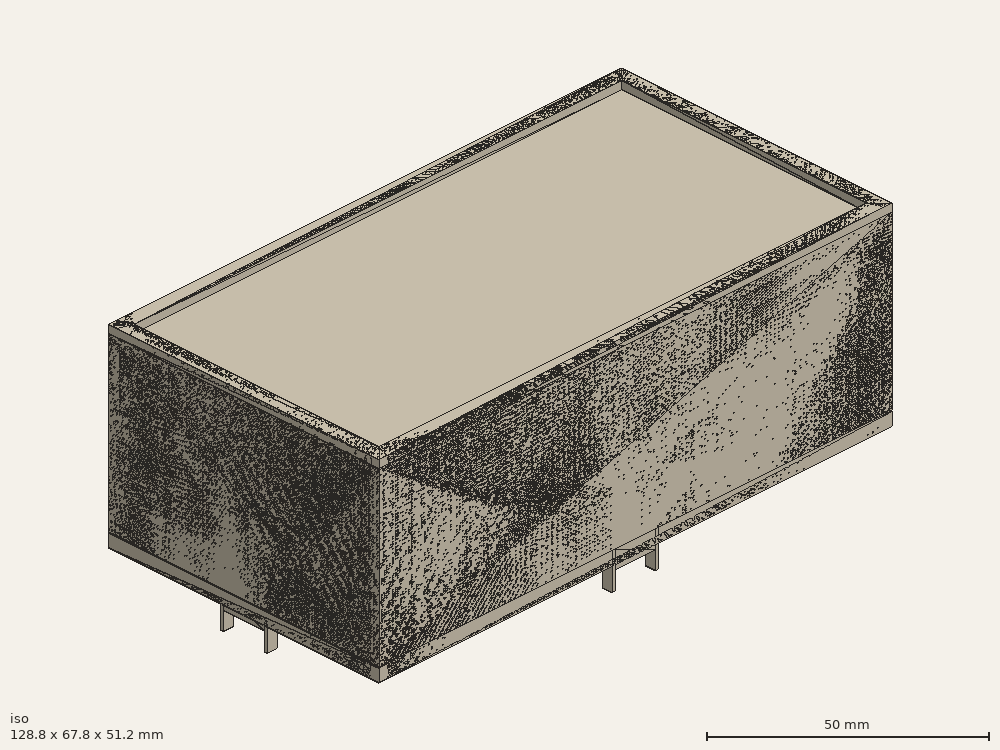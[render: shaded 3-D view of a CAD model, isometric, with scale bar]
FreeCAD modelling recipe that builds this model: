
FCSTD DOCUMENT  (FreeCAD 0.16R6712 (Git))
Label: DesKLOK_case_01
License: All rights reserved
LicenseURL: http://en.wikipedia.org/wiki/All_rights_reserved
objects: Part::Feature×98, Sketcher::SketchObject×19, PartDesign::Pad×15, App::DocumentObjectGroup×5, App::VRMLObject×3, PartDesign::Fillet×3, PartDesign::Pocket×3, Part::MultiFuse×2, PartDesign::LinearPattern×2, Mesh::Feature×1, PartDesign::MultiTransform×1
note: 161 computed .brp shape members not serialized (recipe doc carries the construction recipe); baked Part::Feature solids carry a one-line shape summary decoded from their .brp

FEATURE [App::VRMLObject] ultim8x8
  Placement = pos=(-30.48,0,0) rot=(0,0,1;0rad)
  Resources = ultim8x8/shapes3D/Cap_0805_2012.wrl | ultim8x8/shapes3D/cap_1210_3225M.wrl | ultim8x8/shapes3D/LED_SMD_APA102.wrl
FEATURE [App::VRMLObject] ultim8x8001  label="ultim8x009"
  Placement = pos=(30.48,0,0) rot=(0,0,1;0rad)
  Resources = ultim8x8001/shapes3D/Cap_0805_2012.wrl | ultim8x8001/shapes3D/cap_1210_3225M.wrl | ultim8x8001/shapes3D/LED_SMD_APA102.wrl
FEATURE [App::VRMLObject] ultim_bus_snapped
  Placement = pos=(0,0,-11.6002) rot=(0,1,0;3.14159rad)
  Resources = ultim_bus_snapped/shapes3D/r_0805.wrl
FEATURE [Part::Feature] Part__Feature  label="M0"
  Placement = pos=(-38.1,0,-17.8181) rot=(0.707107,-0.707107,0;3.14159rad)
  shape: bbox 22.93 x 51.59 x 14.94 mm, 1313 faces (baked)
FEATURE [Part::Feature] Part__Feature001  label="cap_elco_R100_D200_H460"
  Placement = pos=(-15.24,22.86,-10.668) rot=(1,0,0;3.14159rad)
  shape: bbox 6.114 x 6.114 x 15.1 mm, 124 faces (baked)
FEATURE [Part::Feature] Part__Feature002  label="User Library-PBS2-16_PBS2_1"
  shape: bbox 2 x 2 x 4.3 mm, 10 faces (baked)
FEATURE [Part::Feature] Part__Feature003  label="User Library-PBS2-16_PBS2_2"
  Placement = pos=(1.75,2.65,0) rot=(0,0,1;0rad)
  shape: bbox 0.7 x 0.7 x 4.3 mm, 10 faces (baked)
FEATURE [Part::Feature] Part__Feature004  label="User Library-PBS2-16_PBS2_3"
  Placement = pos=(2.75,2.75,4.3) rot=(0,0,1;0rad)
  shape: bbox 0.5 x 0.5 x 3.15 mm, 10 faces (baked)
FEATURE [Part::Feature] Part__Feature005  label="User Library-PBS2-16_PBS2_004"
  Placement = pos=(2,0,0) rot=(0,0,1;0rad)
  shape: bbox 2 x 2 x 4.3 mm, 10 faces (baked)
FEATURE [Part::Feature] Part__Feature006  label="User Library-PBS2-16_PBS2_005"
  Placement = pos=(3.75,2.65,0) rot=(0,0,1;0rad)
  shape: bbox 0.7 x 0.7 x 4.3 mm, 10 faces (baked)
FEATURE [Part::Feature] Part__Feature007  label="User Library-PBS2-16_PBS2_006"
  Placement = pos=(4.75,2.75,4.3) rot=(0,0,1;0rad)
  shape: bbox 0.5 x 0.5 x 3.15 mm, 10 faces (baked)
FEATURE [Part::Feature] Part__Feature008  label="User Library-PBS2-16_PBS2_007"
  Placement = pos=(4,0,0) rot=(0,0,1;0rad)
  shape: bbox 2 x 2 x 4.3 mm, 10 faces (baked)
FEATURE [Part::Feature] Part__Feature009  label="User Library-PBS2-16_PBS2_008"
  Placement = pos=(5.75,2.65,0) rot=(0,0,1;0rad)
  shape: bbox 0.7 x 0.7 x 4.3 mm, 10 faces (baked)
FEATURE [Part::Feature] Part__Feature010  label="User Library-PBS2-16_PBS2_009"
  Placement = pos=(6.75,2.75,4.3) rot=(0,0,1;0rad)
  shape: bbox 0.5 x 0.5 x 3.15 mm, 10 faces (baked)
FEATURE [Part::Feature] Part__Feature011  label="User Library-PBS2-16_PBS2_010"
  Placement = pos=(6,0,0) rot=(0,0,1;0rad)
  shape: bbox 2 x 2 x 4.3 mm, 10 faces (baked)
FEATURE [Part::Feature] Part__Feature012  label="User Library-PBS2-16_PBS2_011"
  Placement = pos=(7.75,2.65,0) rot=(0,0,1;0rad)
  shape: bbox 0.7 x 0.7 x 4.3 mm, 10 faces (baked)
FEATURE [Part::Feature] Part__Feature013  label="User Library-PBS2-16_PBS2_012"
  Placement = pos=(8.75,2.75,4.3) rot=(0,0,1;0rad)
  shape: bbox 0.5 x 0.5 x 3.15 mm, 10 faces (baked)
FEATURE [Part::Feature] Part__Feature014  label="User Library-PBS2-16_PBS2_013"
  Placement = pos=(8,0,0) rot=(0,0,1;0rad)
  shape: bbox 2 x 2 x 4.3 mm, 10 faces (baked)
FEATURE [Part::Feature] Part__Feature015  label="User Library-PBS2-16_PBS2_014"
  Placement = pos=(9.75,2.65,0) rot=(0,0,1;0rad)
  shape: bbox 0.7 x 0.7 x 4.3 mm, 10 faces (baked)
FEATURE [Part::Feature] Part__Feature016  label="User Library-PBS2-16_PBS2_015"
  Placement = pos=(10.75,2.75,4.3) rot=(0,0,1;0rad)
  shape: bbox 0.5 x 0.5 x 3.15 mm, 10 faces (baked)
FEATURE [Part::Feature] Part__Feature017  label="User Library-PBS2-16_PBS2_016"
  Placement = pos=(10,0,0) rot=(0,0,1;0rad)
  shape: bbox 2 x 2 x 4.3 mm, 10 faces (baked)
FEATURE [Part::Feature] Part__Feature018  label="User Library-PBS2-16_PBS2_017"
  Placement = pos=(11.75,2.65,0) rot=(0,0,1;0rad)
  shape: bbox 0.7 x 0.7 x 4.3 mm, 10 faces (baked)
FEATURE [Part::Feature] Part__Feature019  label="User Library-PBS2-16_PBS2_018"
  Placement = pos=(12.75,2.75,4.3) rot=(0,0,1;0rad)
  shape: bbox 0.5 x 0.5 x 3.15 mm, 10 faces (baked)
FEATURE [Part::Feature] Part__Feature020  label="User Library-PBS2-16_PBS2_019"
  Placement = pos=(12,0,0) rot=(0,0,1;0rad)
  shape: bbox 2 x 2 x 4.3 mm, 10 faces (baked)
FEATURE [Part::Feature] Part__Feature021  label="User Library-PBS2-16_PBS2_020"
  Placement = pos=(13.75,2.65,0) rot=(0,0,1;0rad)
  shape: bbox 0.7 x 0.7 x 4.3 mm, 10 faces (baked)
FEATURE [Part::Feature] Part__Feature022  label="User Library-PBS2-16_PBS2_021"
  Placement = pos=(14.75,2.75,4.3) rot=(0,0,1;0rad)
  shape: bbox 0.5 x 0.5 x 3.15 mm, 10 faces (baked)
FEATURE [Part::Feature] Part__Feature023  label="User Library-PBS2-16_PBS2_022"
  Placement = pos=(14,0,0) rot=(0,0,1;0rad)
  shape: bbox 2 x 2 x 4.3 mm, 10 faces (baked)
FEATURE [Part::Feature] Part__Feature024  label="User Library-PBS2-16_PBS2_023"
  Placement = pos=(15.75,2.65,0) rot=(0,0,1;0rad)
  shape: bbox 0.7 x 0.7 x 4.3 mm, 10 faces (baked)
FEATURE [Part::Feature] Part__Feature025  label="User Library-PBS2-16_PBS2_024"
  Placement = pos=(16.75,2.75,4.3) rot=(0,0,1;0rad)
  shape: bbox 0.5 x 0.5 x 3.15 mm, 10 faces (baked)
FEATURE [Part::Feature] Part__Feature026  label="User Library-PBS2-16_PBS2_025"
  Placement = pos=(16,0,0) rot=(0,0,1;0rad)
  shape: bbox 2 x 2 x 4.3 mm, 10 faces (baked)
FEATURE [Part::Feature] Part__Feature027  label="User Library-PBS2-16_PBS2_026"
  Placement = pos=(17.75,2.65,0) rot=(0,0,1;0rad)
  shape: bbox 0.7 x 0.7 x 4.3 mm, 10 faces (baked)
FEATURE [Part::Feature] Part__Feature028  label="User Library-PBS2-16_PBS2_027"
  Placement = pos=(18.75,2.75,4.3) rot=(0,0,1;0rad)
  shape: bbox 0.5 x 0.5 x 3.15 mm, 10 faces (baked)
FEATURE [Part::Feature] Part__Feature029  label="User Library-PBS2-16_PBS2_028"
  Placement = pos=(18,0,0) rot=(0,0,1;0rad)
  shape: bbox 2 x 2 x 4.3 mm, 10 faces (baked)
FEATURE [Part::Feature] Part__Feature030  label="User Library-PBS2-16_PBS2_029"
  Placement = pos=(19.75,2.65,0) rot=(0,0,1;0rad)
  shape: bbox 0.7 x 0.7 x 4.3 mm, 10 faces (baked)
FEATURE [Part::Feature] Part__Feature031  label="User Library-PBS2-16_PBS2_030"
  Placement = pos=(20.75,2.75,4.3) rot=(0,0,1;0rad)
  shape: bbox 0.5 x 0.5 x 3.15 mm, 10 faces (baked)
FEATURE [Part::Feature] Part__Feature032  label="User Library-PBS2-16_PBS2_031"
  Placement = pos=(20,0,0) rot=(0,0,1;0rad)
  shape: bbox 2 x 2 x 4.3 mm, 10 faces (baked)
FEATURE [Part::Feature] Part__Feature033  label="User Library-PBS2-16_PBS2_032"
  Placement = pos=(21.75,2.65,0) rot=(0,0,1;0rad)
  shape: bbox 0.7 x 0.7 x 4.3 mm, 10 faces (baked)
FEATURE [Part::Feature] Part__Feature034  label="User Library-PBS2-16_PBS2_033"
  Placement = pos=(22.75,2.75,4.3) rot=(0,0,1;0rad)
  shape: bbox 0.5 x 0.5 x 3.15 mm, 10 faces (baked)
FEATURE [Part::Feature] Part__Feature035  label="User Library-PBS2-16_PBS2_034"
  Placement = pos=(22,0,0) rot=(0,0,1;0rad)
  shape: bbox 2 x 2 x 4.3 mm, 10 faces (baked)
FEATURE [Part::Feature] Part__Feature036  label="User Library-PBS2-16_PBS2_035"
  Placement = pos=(23.75,2.65,0) rot=(0,0,1;0rad)
  shape: bbox 0.7 x 0.7 x 4.3 mm, 10 faces (baked)
FEATURE [Part::Feature] Part__Feature037  label="User Library-PBS2-16_PBS2_036"
  Placement = pos=(24.75,2.75,4.3) rot=(0,0,1;0rad)
  shape: bbox 0.5 x 0.5 x 3.15 mm, 10 faces (baked)
FEATURE [Part::Feature] Part__Feature038  label="User Library-PBS2-16_PBS2_037"
  Placement = pos=(24,0,0) rot=(0,0,1;0rad)
  shape: bbox 2 x 2 x 4.3 mm, 10 faces (baked)
FEATURE [Part::Feature] Part__Feature039  label="User Library-PBS2-16_PBS2_038"
  Placement = pos=(25.75,2.65,0) rot=(0,0,1;0rad)
  shape: bbox 0.7 x 0.7 x 4.3 mm, 10 faces (baked)
FEATURE [Part::Feature] Part__Feature040  label="User Library-PBS2-16_PBS2_039"
  Placement = pos=(26.75,2.75,4.3) rot=(0,0,1;0rad)
  shape: bbox 0.5 x 0.5 x 3.15 mm, 10 faces (baked)
FEATURE [Part::Feature] Part__Feature041  label="User Library-PBS2-16_PBS2_040"
  Placement = pos=(26,0,0) rot=(0,0,1;0rad)
  shape: bbox 2 x 2 x 4.3 mm, 10 faces (baked)
FEATURE [Part::Feature] Part__Feature042  label="User Library-PBS2-16_PBS2_041"
  Placement = pos=(27.75,2.65,0) rot=(0,0,1;0rad)
  shape: bbox 0.7 x 0.7 x 4.3 mm, 10 faces (baked)
FEATURE [Part::Feature] Part__Feature043  label="User Library-PBS2-16_PBS2_042"
  Placement = pos=(28.75,2.75,4.3) rot=(0,0,1;0rad)
  shape: bbox 0.5 x 0.5 x 3.15 mm, 10 faces (baked)
FEATURE [Part::Feature] Part__Feature044  label="User Library-PBS2-16_PBS2_043"
  Placement = pos=(28,0,0) rot=(0,0,1;0rad)
  shape: bbox 2 x 2 x 4.3 mm, 10 faces (baked)
FEATURE [Part::Feature] Part__Feature045  label="User Library-PBS2-16_PBS2_044"
  Placement = pos=(29.75,2.65,0) rot=(0,0,1;0rad)
  shape: bbox 0.7 x 0.7 x 4.3 mm, 10 faces (baked)
FEATURE [Part::Feature] Part__Feature046  label="User Library-PBS2-16_PBS2_045"
  Placement = pos=(30.75,2.75,4.3) rot=(0,0,1;0rad)
  shape: bbox 0.5 x 0.5 x 3.15 mm, 10 faces (baked)
FEATURE [Part::Feature] Part__Feature047  label="User Library-PBS2-16_PBS2_046"
  Placement = pos=(30,0,0) rot=(0,0,1;0rad)
  shape: bbox 2 x 2 x 4.3 mm, 10 faces (baked)
FEATURE [Part::Feature] Part__Feature048  label="User Library-PBS2-16_PBS2_047"
  Placement = pos=(31.75,2.65,0) rot=(0,0,1;0rad)
  shape: bbox 0.7 x 0.7 x 4.3 mm, 10 faces (baked)
FEATURE [Part::Feature] Part__Feature049  label="User Library-PBS2-16_PBS2_048"
  Placement = pos=(32.75,2.75,4.3) rot=(0,0,1;0rad)
  shape: bbox 0.5 x 0.5 x 3.15 mm, 10 faces (baked)
FEATURE [Part::MultiFuse] Fusion  label="header_female_12"
  Placement = pos=(-48.26,-19.05,-15.24) rot=(0,0,1;1.5708rad)
  Shapes = -> [Part__Feature002,Part__Feature003,Part__Feature004,Part__Feature005,Part__Feature006,Part__Feature007,Part__Feature008,Part__Feature009,Part__Feature010,Part__Feature011,Part__Feature012,Part__Feature013,Part__Feature014,Part__Feature015,Part__Feature016,Part__Feature017,Part__Feature018,Part__Feature019,Part__Feature020,Part__Feature021,Part__Feature022,Part__Feature023,Part__Feature024,+25 more]
FEATURE [Part::Feature] Part__Feature050  label="User Library-PBS2-16_PBS2_049"
  shape: bbox 2 x 2 x 4.3 mm, 10 faces (baked)
FEATURE [Part::Feature] Part__Feature051  label="User Library-PBS2-16_PBS2_050"
  Placement = pos=(1.75,2.65,0) rot=(0,0,1;0rad)
  shape: bbox 0.7 x 0.7 x 4.3 mm, 10 faces (baked)
FEATURE [Part::Feature] Part__Feature052  label="User Library-PBS2-16_PBS2_051"
  Placement = pos=(2.75,2.75,4.3) rot=(0,0,1;0rad)
  shape: bbox 0.5 x 0.5 x 3.15 mm, 10 faces (baked)
FEATURE [Part::Feature] Part__Feature053  label="User Library-PBS2-16_PBS2_052"
  Placement = pos=(2,0,0) rot=(0,0,1;0rad)
  shape: bbox 2 x 2 x 4.3 mm, 10 faces (baked)
FEATURE [Part::Feature] Part__Feature054  label="User Library-PBS2-16_PBS2_053"
  Placement = pos=(3.75,2.65,0) rot=(0,0,1;0rad)
  shape: bbox 0.7 x 0.7 x 4.3 mm, 10 faces (baked)
FEATURE [Part::Feature] Part__Feature055  label="User Library-PBS2-16_PBS2_054"
  Placement = pos=(4.75,2.75,4.3) rot=(0,0,1;0rad)
  shape: bbox 0.5 x 0.5 x 3.15 mm, 10 faces (baked)
FEATURE [Part::Feature] Part__Feature056  label="User Library-PBS2-16_PBS2_055"
  Placement = pos=(4,0,0) rot=(0,0,1;0rad)
  shape: bbox 2 x 2 x 4.3 mm, 10 faces (baked)
FEATURE [Part::Feature] Part__Feature057  label="User Library-PBS2-16_PBS2_056"
  Placement = pos=(5.75,2.65,0) rot=(0,0,1;0rad)
  shape: bbox 0.7 x 0.7 x 4.3 mm, 10 faces (baked)
FEATURE [Part::Feature] Part__Feature058  label="User Library-PBS2-16_PBS2_057"
  Placement = pos=(6.75,2.75,4.3) rot=(0,0,1;0rad)
  shape: bbox 0.5 x 0.5 x 3.15 mm, 10 faces (baked)
FEATURE [Part::Feature] Part__Feature059  label="User Library-PBS2-16_PBS2_058"
  Placement = pos=(6,0,0) rot=(0,0,1;0rad)
  shape: bbox 2 x 2 x 4.3 mm, 10 faces (baked)
FEATURE [Part::Feature] Part__Feature060  label="User Library-PBS2-16_PBS2_059"
  Placement = pos=(7.75,2.65,0) rot=(0,0,1;0rad)
  shape: bbox 0.7 x 0.7 x 4.3 mm, 10 faces (baked)
FEATURE [Part::Feature] Part__Feature061  label="User Library-PBS2-16_PBS2_060"
  Placement = pos=(8.75,2.75,4.3) rot=(0,0,1;0rad)
  shape: bbox 0.5 x 0.5 x 3.15 mm, 10 faces (baked)
FEATURE [Part::Feature] Part__Feature062  label="User Library-PBS2-16_PBS2_061"
  Placement = pos=(8,0,0) rot=(0,0,1;0rad)
  shape: bbox 2 x 2 x 4.3 mm, 10 faces (baked)
FEATURE [Part::Feature] Part__Feature063  label="User Library-PBS2-16_PBS2_062"
  Placement = pos=(9.75,2.65,0) rot=(0,0,1;0rad)
  shape: bbox 0.7 x 0.7 x 4.3 mm, 10 faces (baked)
FEATURE [Part::Feature] Part__Feature064  label="User Library-PBS2-16_PBS2_063"
  Placement = pos=(10.75,2.75,4.3) rot=(0,0,1;0rad)
  shape: bbox 0.5 x 0.5 x 3.15 mm, 10 faces (baked)
FEATURE [Part::Feature] Part__Feature065  label="User Library-PBS2-16_PBS2_064"
  Placement = pos=(10,0,0) rot=(0,0,1;0rad)
  shape: bbox 2 x 2 x 4.3 mm, 10 faces (baked)
FEATURE [Part::Feature] Part__Feature066  label="User Library-PBS2-16_PBS2_065"
  Placement = pos=(11.75,2.65,0) rot=(0,0,1;0rad)
  shape: bbox 0.7 x 0.7 x 4.3 mm, 10 faces (baked)
FEATURE [Part::Feature] Part__Feature067  label="User Library-PBS2-16_PBS2_066"
  Placement = pos=(12.75,2.75,4.3) rot=(0,0,1;0rad)
  shape: bbox 0.5 x 0.5 x 3.15 mm, 10 faces (baked)
FEATURE [Part::Feature] Part__Feature068  label="User Library-PBS2-16_PBS2_067"
  Placement = pos=(12,0,0) rot=(0,0,1;0rad)
  shape: bbox 2 x 2 x 4.3 mm, 10 faces (baked)
FEATURE [Part::Feature] Part__Feature069  label="User Library-PBS2-16_PBS2_068"
  Placement = pos=(13.75,2.65,0) rot=(0,0,1;0rad)
  shape: bbox 0.7 x 0.7 x 4.3 mm, 10 faces (baked)
FEATURE [Part::Feature] Part__Feature070  label="User Library-PBS2-16_PBS2_069"
  Placement = pos=(14.75,2.75,4.3) rot=(0,0,1;0rad)
  shape: bbox 0.5 x 0.5 x 3.15 mm, 10 faces (baked)
FEATURE [Part::Feature] Part__Feature071  label="User Library-PBS2-16_PBS2_070"
  Placement = pos=(14,0,0) rot=(0,0,1;0rad)
  shape: bbox 2 x 2 x 4.3 mm, 10 faces (baked)
FEATURE [Part::Feature] Part__Feature072  label="User Library-PBS2-16_PBS2_071"
  Placement = pos=(15.75,2.65,0) rot=(0,0,1;0rad)
  shape: bbox 0.7 x 0.7 x 4.3 mm, 10 faces (baked)
FEATURE [Part::Feature] Part__Feature073  label="User Library-PBS2-16_PBS2_072"
  Placement = pos=(16.75,2.75,4.3) rot=(0,0,1;0rad)
  shape: bbox 0.5 x 0.5 x 3.15 mm, 10 faces (baked)
FEATURE [Part::Feature] Part__Feature074  label="User Library-PBS2-16_PBS2_073"
  Placement = pos=(16,0,0) rot=(0,0,1;0rad)
  shape: bbox 2 x 2 x 4.3 mm, 10 faces (baked)
FEATURE [Part::Feature] Part__Feature075  label="User Library-PBS2-16_PBS2_074"
  Placement = pos=(17.75,2.65,0) rot=(0,0,1;0rad)
  shape: bbox 0.7 x 0.7 x 4.3 mm, 10 faces (baked)
FEATURE [Part::Feature] Part__Feature076  label="User Library-PBS2-16_PBS2_075"
  Placement = pos=(18.75,2.75,4.3) rot=(0,0,1;0rad)
  shape: bbox 0.5 x 0.5 x 3.15 mm, 10 faces (baked)
FEATURE [Part::Feature] Part__Feature077  label="User Library-PBS2-16_PBS2_076"
  Placement = pos=(18,0,0) rot=(0,0,1;0rad)
  shape: bbox 2 x 2 x 4.3 mm, 10 faces (baked)
FEATURE [Part::Feature] Part__Feature078  label="User Library-PBS2-16_PBS2_077"
  Placement = pos=(19.75,2.65,0) rot=(0,0,1;0rad)
  shape: bbox 0.7 x 0.7 x 4.3 mm, 10 faces (baked)
FEATURE [Part::Feature] Part__Feature079  label="User Library-PBS2-16_PBS2_078"
  Placement = pos=(20.75,2.75,4.3) rot=(0,0,1;0rad)
  shape: bbox 0.5 x 0.5 x 3.15 mm, 10 faces (baked)
FEATURE [Part::Feature] Part__Feature080  label="User Library-PBS2-16_PBS2_079"
  Placement = pos=(20,0,0) rot=(0,0,1;0rad)
  shape: bbox 2 x 2 x 4.3 mm, 10 faces (baked)
FEATURE [Part::Feature] Part__Feature081  label="User Library-PBS2-16_PBS2_080"
  Placement = pos=(21.75,2.65,0) rot=(0,0,1;0rad)
  shape: bbox 0.7 x 0.7 x 4.3 mm, 10 faces (baked)
FEATURE [Part::Feature] Part__Feature082  label="User Library-PBS2-16_PBS2_081"
  Placement = pos=(22.75,2.75,4.3) rot=(0,0,1;0rad)
  shape: bbox 0.5 x 0.5 x 3.15 mm, 10 faces (baked)
FEATURE [Part::Feature] Part__Feature083  label="User Library-PBS2-16_PBS2_082"
  Placement = pos=(22,0,0) rot=(0,0,1;0rad)
  shape: bbox 2 x 2 x 4.3 mm, 10 faces (baked)
FEATURE [Part::Feature] Part__Feature084  label="User Library-PBS2-16_PBS2_083"
  Placement = pos=(23.75,2.65,0) rot=(0,0,1;0rad)
  shape: bbox 0.7 x 0.7 x 4.3 mm, 10 faces (baked)
FEATURE [Part::Feature] Part__Feature085  label="User Library-PBS2-16_PBS2_084"
  Placement = pos=(24.75,2.75,4.3) rot=(0,0,1;0rad)
  shape: bbox 0.5 x 0.5 x 3.15 mm, 10 faces (baked)
FEATURE [Part::Feature] Part__Feature086  label="User Library-PBS2-16_PBS2_085"
  Placement = pos=(24,0,0) rot=(0,0,1;0rad)
  shape: bbox 2 x 2 x 4.3 mm, 10 faces (baked)
FEATURE [Part::Feature] Part__Feature087  label="User Library-PBS2-16_PBS2_086"
  Placement = pos=(25.75,2.65,0) rot=(0,0,1;0rad)
  shape: bbox 0.7 x 0.7 x 4.3 mm, 10 faces (baked)
FEATURE [Part::Feature] Part__Feature088  label="User Library-PBS2-16_PBS2_087"
  Placement = pos=(26.75,2.75,4.3) rot=(0,0,1;0rad)
  shape: bbox 0.5 x 0.5 x 3.15 mm, 10 faces (baked)
FEATURE [Part::Feature] Part__Feature089  label="User Library-PBS2-16_PBS2_088"
  Placement = pos=(26,0,0) rot=(0,0,1;0rad)
  shape: bbox 2 x 2 x 4.3 mm, 10 faces (baked)
FEATURE [Part::Feature] Part__Feature090  label="User Library-PBS2-16_PBS2_089"
  Placement = pos=(27.75,2.65,0) rot=(0,0,1;0rad)
  shape: bbox 0.7 x 0.7 x 4.3 mm, 10 faces (baked)
FEATURE [Part::Feature] Part__Feature091  label="User Library-PBS2-16_PBS2_090"
  Placement = pos=(28.75,2.75,4.3) rot=(0,0,1;0rad)
  shape: bbox 0.5 x 0.5 x 3.15 mm, 10 faces (baked)
FEATURE [Part::Feature] Part__Feature092  label="User Library-PBS2-16_PBS2_091"
  Placement = pos=(28,0,0) rot=(0,0,1;0rad)
  shape: bbox 2 x 2 x 4.3 mm, 10 faces (baked)
FEATURE [Part::Feature] Part__Feature093  label="User Library-PBS2-16_PBS2_092"
  Placement = pos=(29.75,2.65,0) rot=(0,0,1;0rad)
  shape: bbox 0.7 x 0.7 x 4.3 mm, 10 faces (baked)
FEATURE [Part::Feature] Part__Feature094  label="User Library-PBS2-16_PBS2_093"
  Placement = pos=(30.75,2.75,4.3) rot=(0,0,1;0rad)
  shape: bbox 0.5 x 0.5 x 3.15 mm, 10 faces (baked)
FEATURE [Part::Feature] Part__Feature095  label="User Library-PBS2-16_PBS2_094"
  Placement = pos=(30,0,0) rot=(0,0,1;0rad)
  shape: bbox 2 x 2 x 4.3 mm, 10 faces (baked)
FEATURE [Part::Feature] Part__Feature096  label="User Library-PBS2-16_PBS2_095"
  Placement = pos=(31.75,2.65,0) rot=(0,0,1;0rad)
  shape: bbox 0.7 x 0.7 x 4.3 mm, 10 faces (baked)
FEATURE [Part::Feature] Part__Feature097  label="User Library-PBS2-16_PBS2_096"
  Placement = pos=(32.75,2.75,4.3) rot=(0,0,1;0rad)
  shape: bbox 0.5 x 0.5 x 3.15 mm, 10 faces (baked)
FEATURE [Part::MultiFuse] Fusion001  label="header_female_16"
  Placement = pos=(-27.94,-19.05,-15.24) rot=(0,0,1;1.5708rad)
  Shapes = -> [Part__Feature050,Part__Feature051,Part__Feature052,Part__Feature053,Part__Feature054,Part__Feature055,Part__Feature056,Part__Feature057,Part__Feature058,Part__Feature059,Part__Feature060,Part__Feature061,Part__Feature062,Part__Feature063,Part__Feature064,Part__Feature065,Part__Feature066,Part__Feature067,Part__Feature068,Part__Feature069,Part__Feature070,Part__Feature071,Part__Feature072,+25 more]
FEATURE [Sketcher::SketchObject] Sketch
  Placement = pos=(0,0,0) rot=(-1,0,0;4.71239rad)
  sketch-geometry (8):
    g0: LineSegment [constr] StartX=-9.99998 StartY=-0.8001 StartZ=0 EndX=0 EndY=-0.8001 EndZ=0
    g1: LineSegment [constr] StartX=0 StartY=-0.8001 StartZ=0 EndX=0 EndY=-10.8001 EndZ=0
    g2: LineSegment [constr] StartX=0 StartY=-10.8001 StartZ=0 EndX=-9.99998 EndY=-10.8001 EndZ=0
    g3: LineSegment [constr] StartX=-9.99998 StartY=-10.8001 StartZ=0 EndX=-9.99998 EndY=-0.8001 EndZ=0
    g4: LineSegment [constr] StartX=-11.9888 StartY=-12.4003 StartZ=0 EndX=0 EndY=-12.4003 EndZ=0
    g5: LineSegment [constr] StartX=0 StartY=-12.4003 StartZ=0 EndX=0 EndY=-24.3891 EndZ=0
    g6: LineSegment [constr] StartX=0 StartY=-24.3891 StartZ=0 EndX=-11.9888 EndY=-24.3891 EndZ=0
    g7: LineSegment [constr] StartX=-11.9888 StartY=-24.3891 StartZ=0 EndX=-11.9888 EndY=-12.4003 EndZ=0
  constraints (24):
    c: Coincident(g0,g1)
    c: Coincident(g1,g2)
    c: Coincident(g2,g3)
    c: Coincident(g3,g0)
    c: Horizontal(g0)
    c: Horizontal(g2)
    c: Vertical(g1)
    c: Vertical(g3)
    c: PointOnObject(g1,g-2)
    c: Coincident(g4,g5)
    c: Coincident(g5,g6)
    c: Coincident(g6,g7)
    c: Coincident(g7,g4)
    c: Horizontal(g4)
    c: Horizontal(g6)
    c: Vertical(g5)
    c: Vertical(g7)
    c: DistanceY(g1,g1) = 9.99998
    c: DistanceY(g5,g5) = 11.9888
    c: Equal(g3,g0)
    c: Equal(g7,g4)
    c: Tangent(g5,g-2) = 1.5708
    c: DistanceY(g0,g-1) = 0.8001
    c: DistanceY(g4,g1) = 1.6002
FEATURE [Mesh::Feature] ultim8x8baffles
  Placement = pos=(-61.3918,30.9118,1.016) rot=(0.707107,0.707107,0;3.14159rad)
FEATURE [Sketcher::SketchObject] Sketch001
  Placement = pos=(0,0,5.4356) rot=(0,0,1;0rad)
  sketch-geometry (4):
    g0: LineSegment StartX=-62.23 StartY=31.75 StartZ=0 EndX=62.23 EndY=31.75 EndZ=0
    g1: LineSegment StartX=62.23 StartY=31.75 StartZ=0 EndX=62.23 EndY=-31.75 EndZ=0
    g2: LineSegment StartX=62.23 StartY=-31.75 StartZ=0 EndX=-62.23 EndY=-31.75 EndZ=0
    g3: LineSegment StartX=-62.23 StartY=-31.75 StartZ=0 EndX=-62.23 EndY=31.75 EndZ=0
  constraints (12):
    c: Coincident(g0,g1)
    c: Coincident(g1,g2)
    c: Coincident(g2,g3)
    c: Coincident(g3,g0)
    c: Horizontal(g0)
    c: Horizontal(g2)
    c: Vertical(g1)
    c: Vertical(g3)
    c: DistanceX(g0,g0) = 124.46
    c: DistanceY(g3,g3) = 63.5
    c: Symmetric(g0,g2,g-1)
    c: Symmetric(g0,g0,g-2)
FEATURE [PartDesign::Pad] Pad  label="Pad_velum"
  Length = 0.1016
  Length2 = 100
  Placement = pos=(0,0,5.4356) rot=(0,0,1;0rad)
  Sketch = -> Sketch001
  Type = 0
FEATURE [Sketcher::SketchObject] Sketch002
  Placement = pos=(0,0,5.5499) rot=(0,0,1;0rad)
  sketch-geometry (4):
    g0: LineSegment StartX=-62.23 StartY=31.75 StartZ=0 EndX=62.23 EndY=31.75 EndZ=0
    g1: LineSegment StartX=62.23 StartY=31.75 StartZ=0 EndX=62.23 EndY=-31.75 EndZ=0
    g2: LineSegment StartX=62.23 StartY=-31.75 StartZ=0 EndX=-62.23 EndY=-31.75 EndZ=0
    g3: LineSegment StartX=-62.23 StartY=-31.75 StartZ=0 EndX=-62.23 EndY=31.75 EndZ=0
  constraints (12):
    c: Coincident(g0,g1)
    c: Coincident(g1,g2)
    c: Coincident(g2,g3)
    c: Coincident(g3,g0)
    c: Horizontal(g0)
    c: Horizontal(g2)
    c: Vertical(g1)
    c: Vertical(g3)
    c: DistanceX(g0,g0) = 124.46
    c: DistanceY(g3,g3) = 63.5
    c: Symmetric(g0,g2,g-1)
    c: Symmetric(g0,g0,g-2)
FEATURE [PartDesign::Pad] Pad001  label="Pad001_acrylic"
  Length = 2.9972
  Length2 = 100
  Placement = pos=(0,0,5.5499) rot=(0,0,1;0rad)
  Sketch = -> Sketch002
  Type = 0
FEATURE [Sketcher::SketchObject] Sketch003
  Placement = pos=(0,0,8.636) rot=(0,0,1;0rad)
  sketch-geometry (8):
    g0: LineSegment StartX=-61.214 StartY=30.734 StartZ=0 EndX=61.214 EndY=30.734 EndZ=0
    g1: LineSegment StartX=61.214 StartY=30.734 StartZ=0 EndX=61.214 EndY=-30.734 EndZ=0
    g2: LineSegment StartX=61.214 StartY=-30.734 StartZ=0 EndX=-61.214 EndY=-30.734 EndZ=0
    g3: LineSegment StartX=-61.214 StartY=-30.734 StartZ=0 EndX=-61.214 EndY=30.734 EndZ=0
    g4: LineSegment StartX=-64.389 StartY=33.909 StartZ=0 EndX=64.389 EndY=33.909 EndZ=0
    g5: LineSegment StartX=64.389 StartY=33.909 StartZ=0 EndX=64.389 EndY=-33.909 EndZ=0
    g6: LineSegment StartX=64.389 StartY=-33.909 StartZ=0 EndX=-64.389 EndY=-33.909 EndZ=0
    g7: LineSegment StartX=-64.389 StartY=-33.909 StartZ=0 EndX=-64.389 EndY=33.909 EndZ=0
  constraints (24):
    c: Coincident(g0,g1)
    c: Coincident(g1,g2)
    c: Coincident(g2,g3)
    c: Coincident(g3,g0)
    c: Horizontal(g0)
    c: Horizontal(g2)
    c: Vertical(g1)
    c: Vertical(g3)
    c: Coincident(g4,g5)
    c: Coincident(g5,g6)
    c: Coincident(g6,g7)
    c: Coincident(g7,g4)
    c: Horizontal(g4)
    c: Horizontal(g6)
    c: Vertical(g5)
    c: Vertical(g7)
    c: Symmetric(g0,g0,g-2)
    c: Symmetric(g0,g1,g-1)
    c: Symmetric(g4,g4,g-2)
    c: Symmetric(g4,g6,g-1)
    c: DistanceY(g1,g1) = 61.468
    c: DistanceX(g2,g1) = 122.428
    c: DistanceX(g0,g4) = 3.175
    c: DistanceY(g0,g4) = 3.175
FEATURE [PartDesign::Pad] Pad002
  Length = 1.905
  Length2 = 100
  Placement = pos=(0,0,8.636) rot=(0,0,1;0rad)
  Sketch = -> Sketch003
  Type = 0
FEATURE [Sketcher::SketchObject] Sketch004
  ExternalGeometry = -> [Pad002]
  Placement = pos=(0,0,8.636) rot=(1,0,0;3.14159rad)
  Support = -> Pad002 [Face9]
  sketch-geometry (8):
    g0: LineSegment StartX=-62.611 StartY=32.131 StartZ=0 EndX=62.611 EndY=32.131 EndZ=0
    g1: LineSegment StartX=62.611 StartY=32.131 StartZ=0 EndX=62.611 EndY=-32.131 EndZ=0
    g2: LineSegment StartX=62.611 StartY=-32.131 StartZ=0 EndX=-62.611 EndY=-32.131 EndZ=0
    g3: LineSegment StartX=-62.611 StartY=-32.131 StartZ=0 EndX=-62.611 EndY=32.131 EndZ=0
    g4: LineSegment StartX=-64.389 StartY=33.909 StartZ=0 EndX=64.389 EndY=33.909 EndZ=0
    g5: LineSegment StartX=64.389 StartY=33.909 StartZ=0 EndX=64.389 EndY=-33.909 EndZ=0
    g6: LineSegment StartX=64.389 StartY=-33.909 StartZ=0 EndX=-64.389 EndY=-33.909 EndZ=0
    g7: LineSegment StartX=-64.389 StartY=-33.909 StartZ=0 EndX=-64.389 EndY=33.909 EndZ=0
  constraints (22):
    c: Coincident(g0,g1)
    c: Coincident(g1,g2)
    c: Coincident(g2,g3)
    c: Coincident(g3,g0)
    c: Horizontal(g0)
    c: Horizontal(g2)
    c: Vertical(g1)
    c: Vertical(g3)
    c: Coincident(g4,g5)
    c: Coincident(g5,g6)
    c: Coincident(g6,g7)
    c: Coincident(g7,g4)
    c: Horizontal(g4)
    c: Horizontal(g6)
    c: Vertical(g5)
    c: Vertical(g7)
    c: Coincident(g4,g-3)
    c: Coincident(g-4,g5)
    c: Symmetric(g0,g0,g-2)
    c: Symmetric(g0,g2,g-1)
    c: DistanceX(g4,g0) = 1.778
    c: DistanceY(g0,g4) = 1.778
FEATURE [PartDesign::Pad] Pad003
  Length = 40.64
  Length2 = 100
  Placement = pos=(0,0,8.636) rot=(0,0,1;0rad)
  Sketch = -> Sketch004
  Type = 0
FEATURE [Sketcher::SketchObject] Sketch005
  Placement = pos=(0,0,-32.258) rot=(1,0,0;3.14159rad)
  sketch-geometry (4):
    g0: LineSegment StartX=-64.389 StartY=33.909 StartZ=0 EndX=64.389 EndY=33.909 EndZ=0
    g1: LineSegment StartX=64.389 StartY=33.909 StartZ=0 EndX=64.389 EndY=-33.909 EndZ=0
    g2: LineSegment StartX=64.389 StartY=-33.909 StartZ=0 EndX=-64.389 EndY=-33.909 EndZ=0
    g3: LineSegment StartX=-64.389 StartY=-33.909 StartZ=0 EndX=-64.389 EndY=33.909 EndZ=0
  constraints (12):
    c: Coincident(g0,g1)
    c: Coincident(g1,g2)
    c: Coincident(g2,g3)
    c: Coincident(g3,g0)
    c: Horizontal(g0)
    c: Horizontal(g2)
    c: Vertical(g1)
    c: Vertical(g3)
    c: Symmetric(g0,g0,g-2)
    c: Symmetric(g0,g2,g-1)
    c: DistanceX(g0,g0) = 128.778
    c: DistanceY(g3,g3) = 67.818
FEATURE [PartDesign::Pad] Pad004
  Length = 2.9972
  Length2 = 100
  Placement = pos=(0,0,-32.258) rot=(1,0,0;3.14159rad)
  Sketch = -> Sketch005
  Type = 0
FEATURE [Sketcher::SketchObject] Sketch006
  ExternalGeometry = -> [Pad004]
  Placement = pos=(0,0,-32.258) rot=(0,0,1;0rad)
  Support = -> Pad004 [Face5]
  sketch-geometry (16):
    g0: LineSegment StartX=-38.1 StartY=-28.575 StartZ=0 EndX=-27.94 EndY=-28.575 EndZ=0
    g1: LineSegment StartX=-27.94 StartY=-28.575 StartZ=0 EndX=-27.94 EndY=-31.115 EndZ=0
    g2: LineSegment StartX=-27.94 StartY=-31.115 StartZ=0 EndX=-38.1 EndY=-31.115 EndZ=0
    g3: LineSegment StartX=-38.1 StartY=-31.115 StartZ=0 EndX=-38.1 EndY=-28.575 EndZ=0
    g4: LineSegment StartX=27.94 StartY=-28.575 StartZ=0 EndX=38.1 EndY=-28.575 EndZ=0
    g5: LineSegment StartX=38.1 StartY=-28.575 StartZ=0 EndX=38.1 EndY=-31.115 EndZ=0
    g6: LineSegment StartX=38.1 StartY=-31.115 StartZ=0 EndX=27.94 EndY=-31.115 EndZ=0
    g7: LineSegment StartX=27.94 StartY=-31.115 StartZ=0 EndX=27.94 EndY=-28.575 EndZ=0
    g8: LineSegment StartX=27.94 StartY=31.115 StartZ=0 EndX=38.1 EndY=31.115 EndZ=0
    g9: LineSegment StartX=38.1 StartY=31.115 StartZ=0 EndX=38.1 EndY=28.575 EndZ=0
    g10: LineSegment StartX=38.1 StartY=28.575 StartZ=0 EndX=27.94 EndY=28.575 EndZ=0
    g11: LineSegment StartX=27.94 StartY=28.575 StartZ=0 EndX=27.94 EndY=31.115 EndZ=0
    g12: LineSegment StartX=-38.1 StartY=31.115 StartZ=0 EndX=-27.94 EndY=31.115 EndZ=0
    g13: LineSegment StartX=-27.94 StartY=31.115 StartZ=0 EndX=-27.94 EndY=28.575 EndZ=0
    g14: LineSegment StartX=-27.94 StartY=28.575 StartZ=0 EndX=-38.1 EndY=28.575 EndZ=0
    g15: LineSegment StartX=-38.1 StartY=28.575 StartZ=0 EndX=-38.1 EndY=31.115 EndZ=0
  constraints (45):
    c: Coincident(g0,g1)
    c: Coincident(g1,g2)
    c: Coincident(g2,g3)
    c: Coincident(g3,g0)
    c: Horizontal(g0)
    c: Horizontal(g2)
    c: Vertical(g1)
    c: Vertical(g3)
    c: Coincident(g4,g5)
    c: Coincident(g5,g6)
    c: Coincident(g6,g7)
    c: Coincident(g7,g4)
    c: Horizontal(g4)
    c: Horizontal(g6)
    c: Vertical(g5)
    c: Vertical(g7)
    c: Coincident(g8,g9)
    c: Coincident(g9,g10)
    c: Coincident(g10,g11)
    c: Coincident(g11,g8)
    c: Horizontal(g8)
    c: Horizontal(g10)
    c: Vertical(g9)
    c: Vertical(g11)
    c: Coincident(g12,g13)
    c: Coincident(g13,g14)
    c: Coincident(g14,g15)
    c: Coincident(g15,g12)
    c: Horizontal(g12)
    c: Horizontal(g14)
    c: Vertical(g13)
    c: Vertical(g15)
    c: Equal(g14,g10)
    c: Equal(g10,g4)
    c: Equal(g4,g0)
    c: Equal(g13,g11)
    c: Equal(g11,g7)
    c: Equal(g7,g1)
    c: DistanceX(g14,g14) = 10.16
    c: DistanceY(g13,g13) = 2.54
    c: Symmetric(g13,g10,g-2)
    c: Symmetric(g0,g4,g-2)
    c: Symmetric(g13,g0,g-1)
    c: DistanceY(g2,g12) = 62.23
    c: DistanceX(g2,g5) = 76.2
FEATURE [PartDesign::Pad] Pad005
  Length = 10.16
  Length2 = 100
  Placement = pos=(0,0,-32.258) rot=(1,0,0;3.14159rad)
  Sketch = -> Sketch006
  Type = 0
FEATURE [Sketcher::SketchObject] Sketch007
  ExternalGeometry = -> [Pad005]
  Placement = pos=(38.1,0,-32.258) rot=(-0.57735,0.57735,-0.57735;2.0944rad)
  Support = -> Pad005 [Face22]
  sketch-geometry (2):
    g0: Circle CenterX=-30.48 CenterY=-8.255 CenterZ=0 NormalX=0 NormalY=0 NormalZ=1 Radius=1.905
    g1: Circle CenterX=30.48 CenterY=-8.255 CenterZ=0 NormalX=0 NormalY=0 NormalZ=1 Radius=1.905
  constraints (5):
    c: Symmetric(g0,g1,g-2)
    c: Equal(g0,g1)
    c: Tangent(g0,g-4)
    c: Tangent(g0,g-3)
    c: Radius(g0) = 1.905
FEATURE [PartDesign::Pad] Pad006
  Length = 10
  Length2 = 100
  Placement = pos=(0,0,-32.258) rot=(1,0,0;3.14159rad)
  Reversed = true
  Sketch = -> Sketch007
  Type = 3
  UpToFace = -> Pad005 [Face20]
FEATURE [Sketcher::SketchObject] Sketch008
  ExternalGeometry = -> [Pad006]
  Placement = pos=(-38.1,0,-32.258) rot=(0.57735,0.57735,-0.57735;4.18879rad)
  Support = -> Pad006 [Face10]
  sketch-geometry (2):
    g0: Circle CenterX=-30.48 CenterY=-8.255 CenterZ=0 NormalX=0 NormalY=0 NormalZ=1 Radius=1.905
    g1: Circle CenterX=30.48 CenterY=-8.255 CenterZ=0 NormalX=0 NormalY=0 NormalZ=1 Radius=1.905
  constraints (5):
    c: Symmetric(g0,g1,g-2)
    c: Equal(g0,g1)
    c: Radius(g0) = 1.905
    c: Tangent(g0,g-3)
    c: Tangent(g0,g-4)
FEATURE [PartDesign::Pad] Pad007
  Length = 10
  Length2 = 100
  Placement = pos=(0,0,-32.258) rot=(1,0,0;3.14159rad)
  Reversed = true
  Sketch = -> Sketch008
  Type = 3
  UpToFace = -> Pad006 [Face11]
FEATURE [Sketcher::SketchObject] Sketch009
  Placement = pos=(0,0,-32.004) rot=(1,0,0;3.14159rad)
  Support = -> Pad003 [Face15]
  expr: Constraints[43] = 4.8in + 0.02in + 0.125in + 0.125in
  expr: Constraints[44] = 2.4in + 0.02in + 0.125in + 0.125in
  sketch-geometry (16):
    g0: LineSegment StartX=-5.08 StartY=33.909 StartZ=0 EndX=5.08 EndY=33.909 EndZ=0
    g1: LineSegment StartX=5.08 StartY=33.909 StartZ=0 EndX=5.08 EndY=32.131 EndZ=0
    g2: LineSegment StartX=5.08 StartY=32.131 StartZ=0 EndX=-5.08 EndY=32.131 EndZ=0
    g3: LineSegment StartX=-5.08 StartY=32.131 StartZ=0 EndX=-5.08 EndY=33.909 EndZ=0
    g4: LineSegment StartX=-5.08 StartY=-33.909 StartZ=0 EndX=5.08 EndY=-33.909 EndZ=0
    g5: LineSegment StartX=5.08 StartY=-33.909 StartZ=0 EndX=5.08 EndY=-32.131 EndZ=0
    g6: LineSegment StartX=5.08 StartY=-32.131 StartZ=0 EndX=-5.08 EndY=-32.131 EndZ=0
    g7: LineSegment StartX=-5.08 StartY=-32.131 StartZ=0 EndX=-5.08 EndY=-33.909 EndZ=0
    g8: LineSegment StartX=-64.389 StartY=5.08 StartZ=0 EndX=-62.611 EndY=5.08 EndZ=0
    g9: LineSegment StartX=-62.611 StartY=5.08 StartZ=0 EndX=-62.611 EndY=-5.08 EndZ=0
    g10: LineSegment StartX=-62.611 StartY=-5.08 StartZ=0 EndX=-64.389 EndY=-5.08 EndZ=0
    g11: LineSegment StartX=-64.389 StartY=-5.08 StartZ=0 EndX=-64.389 EndY=5.08 EndZ=0
    g12: LineSegment StartX=62.611 StartY=5.08 StartZ=0 EndX=64.389 EndY=5.08 EndZ=0
    g13: LineSegment StartX=64.389 StartY=5.08 StartZ=0 EndX=64.389 EndY=-5.08 EndZ=0
    g14: LineSegment StartX=64.389 StartY=-5.08 StartZ=0 EndX=62.611 EndY=-5.08 EndZ=0
    g15: LineSegment StartX=62.611 StartY=-5.08 StartZ=0 EndX=62.611 EndY=5.08 EndZ=0
  constraints (46):
    c: Coincident(g0,g1)
    c: Coincident(g1,g2)
    c: Coincident(g2,g3)
    c: Coincident(g3,g0)
    c: Horizontal(g0)
    c: Horizontal(g2)
    c: Vertical(g1)
    c: Vertical(g3)
    c: Coincident(g4,g5)
    c: Coincident(g5,g6)
    c: Coincident(g6,g7)
    c: Coincident(g7,g4)
    c: Horizontal(g4)
    c: Horizontal(g6)
    c: Vertical(g5)
    c: Vertical(g7)
    c: Coincident(g8,g9)
    c: Coincident(g9,g10)
    c: Coincident(g10,g11)
    c: Coincident(g11,g8)
    c: Horizontal(g8)
    c: Horizontal(g10)
    c: Vertical(g9)
    c: Vertical(g11)
    c: Coincident(g12,g13)
    c: Coincident(g13,g14)
    c: Coincident(g14,g15)
    c: Coincident(g15,g12)
    c: Horizontal(g12)
    c: Horizontal(g14)
    c: Vertical(g13)
    c: Vertical(g15)
    c: Equal(g2,g15)
    c: Equal(g15,g4)
    c: Equal(g4,g9)
    c: Equal(g8,g1)
    c: Equal(g1,g14)
    c: Equal(g14,g7)
    c: Symmetric(g8,g12,g-2)
    c: Symmetric(g8,g9,g-1)
    c: Symmetric(g2,g1,g-2)
    c: DistanceY(g15,g15) = 10.16
    c: DistanceX(g12,g12) = 1.778
    c: DistanceX(g8,g12) = 128.778
    c: DistanceY(g4,g0) = 67.818
    c: Symmetric(g4,g0,g-1)
FEATURE [PartDesign::Pad] Pad008
  Length = 4.318
  Length2 = 100
  Placement = pos=(0,0,8.636) rot=(0,0,1;0rad)
  Sketch = -> Sketch009
  Type = 0
FEATURE [Sketcher::SketchObject] Sketch010
  ExternalGeometry = -> [Pad008]
  Placement = pos=(-5.08,0,8.636) rot=(0.57735,-0.57735,-0.57735;2.0944rad)
  Support = -> Pad008 [Face29]
  sketch-geometry (6):
    g0: LineSegment StartX=-32.131 StartY=-44.958 StartZ=0 EndX=-32.131 EndY=-43.688 EndZ=0
    g1: LineSegment StartX=-32.131 StartY=-43.688 StartZ=0 EndX=-31.115 EndY=-43.688 EndZ=0
    g2: LineSegment StartX=-31.115 StartY=-43.688 StartZ=0 EndX=-32.131 EndY=-44.958 EndZ=0
    g3: LineSegment StartX=32.131 StartY=-44.958 StartZ=0 EndX=32.131 EndY=-43.688 EndZ=0
    g4: LineSegment StartX=32.131 StartY=-43.688 StartZ=0 EndX=31.115 EndY=-43.688 EndZ=0
    g5: LineSegment StartX=31.115 StartY=-43.688 StartZ=0 EndX=32.131 EndY=-44.958 EndZ=0
  constraints (16):
    c: Vertical(g0)
    c: Coincident(g0,g1)
    c: Horizontal(g1)
    c: Coincident(g1,g2)
    c: Vertical(g3)
    c: Coincident(g3,g4)
    c: Horizontal(g4)
    c: Coincident(g4,g5)
    c: Coincident(g5,g3)
    c: Coincident(g0,g2)
    c: Equal(g0,g3)
    c: Equal(g1,g4)
    c: Symmetric(g3,g0,g-2)
    c: DistanceY(g0,g0) = 1.27
    c: DistanceX(g1,g1) = 1.016
    c: Coincident(g0,g-3)
FEATURE [PartDesign::Pad] Pad009
  Length = 10
  Length2 = 100
  Placement = pos=(0,0,8.636) rot=(0,0,1;0rad)
  Reversed = true
  Sketch = -> Sketch010
  Type = 3
  UpToFace = -> Pad008 [Face27]
FEATURE [Sketcher::SketchObject] Sketch011
  ExternalGeometry = -> [Pad009]
  Placement = pos=(0,-5.08,8.636) rot=(1,0,0;1.5708rad)
  Support = -> Pad009 [Face36]
  sketch-geometry (6):
    g0: LineSegment StartX=-62.611 StartY=-44.958 StartZ=0 EndX=-62.611 EndY=-43.688 EndZ=0
    g1: LineSegment StartX=-62.611 StartY=-43.688 StartZ=0 EndX=-61.595 EndY=-43.688 EndZ=0
    g2: LineSegment StartX=-61.595 StartY=-43.688 StartZ=0 EndX=-62.611 EndY=-44.958 EndZ=0
    g3: LineSegment StartX=62.611 StartY=-44.958 StartZ=0 EndX=62.611 EndY=-43.688 EndZ=0
    g4: LineSegment StartX=62.611 StartY=-43.688 StartZ=0 EndX=61.595 EndY=-43.688 EndZ=0
    g5: LineSegment StartX=61.595 StartY=-43.688 StartZ=0 EndX=62.611 EndY=-44.958 EndZ=0
  constraints (16):
    c: Vertical(g0)
    c: Coincident(g0,g1)
    c: Horizontal(g1)
    c: Coincident(g1,g2)
    c: Vertical(g3)
    c: Coincident(g3,g4)
    c: Horizontal(g4)
    c: Coincident(g4,g5)
    c: Coincident(g5,g3)
    c: Coincident(g0,g2)
    c: DistanceY(g0,g0) = 1.27
    c: DistanceX(g1,g1) = 1.016
    c: Symmetric(g3,g0,g-2)
    c: Coincident(g0,g-3)
    c: DistanceX(g4,g4) = 1.016
    c: DistanceY(g3,g3) = 1.27
FEATURE [PartDesign::Pad] Pad010
  Length = 10
  Length2 = 100
  Placement = pos=(0,0,8.636) rot=(0,0,1;0rad)
  Reversed = true
  Sketch = -> Sketch011
  Type = 3
  UpToFace = -> Pad009 [Face31]
FEATURE [App::DocumentObjectGroup] Group002  label="3d_models"
  Group = -> [ultim8x8,ultim8x8001,ultim_bus_snapped,Part__Feature,Part__Feature001,Fusion,Fusion001]
FEATURE [App::DocumentObjectGroup] Group003  label="front_parts"
  Group = -> [Pad,Pad001]
FEATURE [Sketcher::SketchObject] Sketch012
  Placement = pos=(0,0,-32.004) rot=(1,0,0;3.14159rad)
  expr: Constraints[55] = 2.4in + 0.02in + 0.125in + 0.125in
  expr: Constraints[54] = 4.8in + 0.02in + 0.125in + 0.125in
  sketch-geometry (20):
    g0: LineSegment StartX=-64.389 StartY=33.909 StartZ=0 EndX=-5.334 EndY=33.909 EndZ=0
    g1: LineSegment StartX=-5.334 StartY=33.909 StartZ=0 EndX=-5.334 EndY=31.877 EndZ=0
    g2: LineSegment StartX=-5.334 StartY=31.877 StartZ=0 EndX=5.334 EndY=31.877 EndZ=0
    g3: LineSegment StartX=5.334 StartY=31.877 StartZ=0 EndX=5.334 EndY=33.909 EndZ=0
    g4: LineSegment StartX=5.334 StartY=33.909 StartZ=0 EndX=64.389 EndY=33.909 EndZ=0
    g5: LineSegment StartX=64.389 StartY=33.909 StartZ=0 EndX=64.389 EndY=5.334 EndZ=0
    g6: LineSegment StartX=64.389 StartY=5.334 StartZ=0 EndX=62.357 EndY=5.334 EndZ=0
    g7: LineSegment StartX=62.357 StartY=5.334 StartZ=0 EndX=62.357 EndY=-5.334 EndZ=0
    g8: LineSegment StartX=62.357 StartY=-5.334 StartZ=0 EndX=64.389 EndY=-5.334 EndZ=0
    g9: LineSegment StartX=64.389 StartY=-5.334 StartZ=0 EndX=64.389 EndY=-33.909 EndZ=0
    g10: LineSegment StartX=64.389 StartY=-33.909 StartZ=0 EndX=5.334 EndY=-33.909 EndZ=0
    g11: LineSegment StartX=5.334 StartY=-33.909 StartZ=0 EndX=5.334 EndY=-31.877 EndZ=0
    g12: LineSegment StartX=5.334 StartY=-31.877 StartZ=0 EndX=-5.334 EndY=-31.877 EndZ=0
    g13: LineSegment StartX=-5.334 StartY=-31.877 StartZ=0 EndX=-5.334 EndY=-33.909 EndZ=0
    g14: LineSegment StartX=-5.334 StartY=-33.909 StartZ=0 EndX=-64.389 EndY=-33.909 EndZ=0
    g15: LineSegment StartX=-64.389 StartY=-33.909 StartZ=0 EndX=-64.389 EndY=-5.334 EndZ=0
    g16: LineSegment StartX=-64.389 StartY=-5.334 StartZ=0 EndX=-62.357 EndY=-5.334 EndZ=0
    g17: LineSegment StartX=-62.357 StartY=-5.334 StartZ=0 EndX=-62.357 EndY=5.334 EndZ=0
    g18: LineSegment StartX=-62.357 StartY=5.334 StartZ=0 EndX=-64.389 EndY=5.334 EndZ=0
    g19: LineSegment StartX=-64.389 StartY=5.334 StartZ=0 EndX=-64.389 EndY=33.909 EndZ=0
  constraints (60):
    c: Horizontal(g0)
    c: Coincident(g0,g1)
    c: Coincident(g1,g2)
    c: Horizontal(g2)
    c: Coincident(g2,g3)
    c: Vertical(g3)
    c: Coincident(g3,g4)
    c: Horizontal(g4)
    c: Coincident(g4,g5)
    c: Vertical(g5)
    c: Coincident(g5,g6)
    c: Coincident(g6,g7)
    c: Vertical(g7)
    c: Coincident(g7,g8)
    c: Coincident(g8,g9)
    c: Vertical(g9)
    c: Coincident(g9,g10)
    c: Horizontal(g10)
    c: Coincident(g10,g11)
    c: Coincident(g11,g12)
    c: Horizontal(g12)
    c: Coincident(g12,g13)
    c: Coincident(g13,g14)
    c: Horizontal(g14)
    c: Coincident(g14,g15)
    c: Vertical(g15)
    c: Coincident(g15,g16)
    c: Horizontal(g16)
    c: Coincident(g16,g17)
    c: Vertical(g17)
    c: Coincident(g17,g18)
    c: Horizontal(g18)
    c: Coincident(g18,g19)
    c: Coincident(g19,g0)
    c: Vertical(g1)
    c: Horizontal(g6)
    c: Horizontal(g8)
    c: Vertical(g11)
    c: Vertical(g13)
    c: Vertical(g19)
    c: Equal(g1,g3)
    c: Equal(g3,g13)
    c: Equal(g13,g11)
    c: Equal(g6,g8)
    c: Equal(g8,g16)
    c: Equal(g16,g18)
    c: Equal(g2,g12)
    c: Equal(g17,g7)
    c: Symmetric(g17,g16,g-1)
    c: Symmetric(g6,g7,g-1)
    c: Symmetric(g1,g2,g-2)
    c: Symmetric(g12,g11,g-2)
    c: Symmetric(g17,g6,g-2)
    c: Symmetric(g1,g12,g-1)
    c: DistanceX(g0,g4) = 128.778
    c: DistanceY(g14,g0) = 67.818
    c: DistanceY(g17,g17) = 10.668
    c: DistanceX(g2,g2) = 10.668
    c: DistanceX(g18,g18) = 2.032
    c: DistanceY(g1,g1) = 2.032
FEATURE [PartDesign::Pad] Pad011
  Length = 2.9972
  Length2 = 100
  Placement = pos=(0,0,-32.004) rot=(1,0,0;3.14159rad)
  Sketch = -> Sketch012
  Type = 0
FEATURE [PartDesign::Fillet] Fillet
  Base = -> Pad011 [Edge14,Edge29,Edge44,Edge1]
  Placement = pos=(0,0,-32.004) rot=(1,0,0;3.14159rad)
  Radius = 2.032
FEATURE [App::DocumentObjectGroup] Group001  label="back_cover"
  Group = -> [Pad004,Pad005,Pad006,Pad007,Pad011,Fillet]
FEATURE [PartDesign::Fillet] Fillet001
  Base = -> Pad010 [Edge13,Edge30,Edge11,Edge25,Edge27,Edge9,Edge34,Edge15]
  Placement = pos=(0,0,8.636) rot=(0,0,1;0rad)
  Radius = 2.032
FEATURE [Sketcher::SketchObject] Sketch013
  Placement = pos=(0,0,-32.004) rot=(1,0,0;3.14159rad)
  Support = -> Fillet001 [Face26]
  expr: Constraints[105] = 2.4in + 0.02in + 0.125in + 0.125in
  expr: Constraints[83] = 4.8in + 0.02in + 0.125in + 0.125in
  sketch-geometry (32):
    g0: LineSegment StartX=-5.842 StartY=33.909 StartZ=0 EndX=-5.08 EndY=33.909 EndZ=0
    g1: LineSegment StartX=-5.08 StartY=33.909 StartZ=0 EndX=-5.08 EndY=31.369 EndZ=0
    g2: LineSegment StartX=-5.08 StartY=31.369 StartZ=0 EndX=-5.842 EndY=31.369 EndZ=0
    g3: LineSegment StartX=-5.842 StartY=31.369 StartZ=0 EndX=-5.842 EndY=33.909 EndZ=0
    g4: LineSegment StartX=5.08 StartY=31.369 StartZ=0 EndX=5.842 EndY=31.369 EndZ=0
    g5: LineSegment StartX=5.842 StartY=31.369 StartZ=0 EndX=5.842 EndY=33.909 EndZ=0
    g6: LineSegment StartX=5.842 StartY=33.909 StartZ=0 EndX=5.08 EndY=33.909 EndZ=0
    g7: LineSegment StartX=5.08 StartY=33.909 StartZ=0 EndX=5.08 EndY=31.369 EndZ=0
    g8: LineSegment StartX=-5.08 StartY=-31.369 StartZ=0 EndX=-5.842 EndY=-31.369 EndZ=0
    g9: LineSegment StartX=-5.842 StartY=-31.369 StartZ=0 EndX=-5.842 EndY=-33.909 EndZ=0
    g10: LineSegment StartX=-5.842 StartY=-33.909 StartZ=0 EndX=-5.08 EndY=-33.909 EndZ=0
    g11: LineSegment StartX=-5.08 StartY=-33.909 StartZ=0 EndX=-5.08 EndY=-31.369 EndZ=0
    g12: LineSegment StartX=5.08 StartY=-31.369 StartZ=0 EndX=5.842 EndY=-31.369 EndZ=0
    g13: LineSegment StartX=5.842 StartY=-31.369 StartZ=0 EndX=5.842 EndY=-33.909 EndZ=0
    g14: LineSegment StartX=5.842 StartY=-33.909 StartZ=0 EndX=5.08 EndY=-33.909 EndZ=0
    g15: LineSegment StartX=5.08 StartY=-33.909 StartZ=0 EndX=5.08 EndY=-31.369 EndZ=0
    g16: LineSegment StartX=-61.849 StartY=5.08 StartZ=0 EndX=-64.389 EndY=5.08 EndZ=0
    g17: LineSegment StartX=-64.389 StartY=5.08 StartZ=0 EndX=-64.389 EndY=5.842 EndZ=0
    g18: LineSegment StartX=-64.389 StartY=5.842 StartZ=0 EndX=-61.849 EndY=5.842 EndZ=0
    g19: LineSegment StartX=-61.849 StartY=5.842 StartZ=0 EndX=-61.849 EndY=5.08 EndZ=0
    g20: LineSegment StartX=-61.849 StartY=-5.08 StartZ=0 EndX=-64.389 EndY=-5.08 EndZ=0
    g21: LineSegment StartX=-64.389 StartY=-5.08 StartZ=0 EndX=-64.389 EndY=-5.842 EndZ=0
    g22: LineSegment StartX=-64.389 StartY=-5.842 StartZ=0 EndX=-61.849 EndY=-5.842 EndZ=0
    g23: LineSegment StartX=-61.849 StartY=-5.842 StartZ=0 EndX=-61.849 EndY=-5.08 EndZ=0
    g24: LineSegment StartX=61.849 StartY=5.08 StartZ=0 EndX=64.389 EndY=5.08 EndZ=0
    g25: LineSegment StartX=64.389 StartY=5.08 StartZ=0 EndX=64.389 EndY=5.842 EndZ=0
    g26: LineSegment StartX=64.389 StartY=5.842 StartZ=0 EndX=61.849 EndY=5.842 EndZ=0
    g27: LineSegment StartX=61.849 StartY=5.842 StartZ=0 EndX=61.849 EndY=5.08 EndZ=0
    g28: LineSegment StartX=61.849 StartY=-5.08 StartZ=0 EndX=64.389 EndY=-5.08 EndZ=0
    g29: LineSegment StartX=64.389 StartY=-5.08 StartZ=0 EndX=64.389 EndY=-5.842 EndZ=0
    g30: LineSegment StartX=64.389 StartY=-5.842 StartZ=0 EndX=61.849 EndY=-5.842 EndZ=0
    g31: LineSegment StartX=61.849 StartY=-5.842 StartZ=0 EndX=61.849 EndY=-5.08 EndZ=0
  constraints (106):
    c: Coincident(g0,g1)
    c: Coincident(g1,g2)
    c: Coincident(g2,g3)
    c: Coincident(g3,g0)
    c: Horizontal(g0)
    c: Horizontal(g2)
    c: Vertical(g1)
    c: Vertical(g3)
    c: Coincident(g4,g5)
    c: Coincident(g5,g6)
    c: Coincident(g6,g7)
    c: Coincident(g7,g4)
    c: Horizontal(g4)
    c: Horizontal(g6)
    c: Vertical(g5)
    c: Vertical(g7)
    c: Coincident(g8,g9)
    c: Coincident(g9,g10)
    c: Coincident(g10,g11)
    c: Coincident(g11,g8)
    c: Horizontal(g8)
    c: Horizontal(g10)
    c: Vertical(g9)
    c: Vertical(g11)
    c: Coincident(g12,g13)
    c: Coincident(g13,g14)
    c: Coincident(g14,g15)
    c: Coincident(g15,g12)
    c: Horizontal(g12)
    c: Horizontal(g14)
    c: Vertical(g13)
    c: Vertical(g15)
    c: Coincident(g16,g17)
    c: Coincident(g17,g18)
    c: Coincident(g18,g19)
    c: Coincident(g19,g16)
    c: Horizontal(g16)
    c: Horizontal(g18)
    c: Vertical(g17)
    c: Vertical(g19)
    c: Coincident(g20,g21)
    c: Coincident(g21,g22)
    c: Coincident(g22,g23)
    c: Coincident(g23,g20)
    c: Horizontal(g20)
    c: Horizontal(g22)
    c: Vertical(g21)
    c: Vertical(g23)
    c: Coincident(g24,g25)
    c: Coincident(g25,g26)
    c: Coincident(g26,g27)
    c: Coincident(g27,g24)
    c: Horizontal(g24)
    c: Horizontal(g26)
    c: Vertical(g25)
    c: Vertical(g27)
    c: Coincident(g28,g29)
    c: Coincident(g29,g30)
    c: Coincident(g30,g31)
    c: Coincident(g31,g28)
    c: Horizontal(g28)
    c: Horizontal(g30)
    c: Vertical(g29)
    c: Vertical(g31)
    c: Equal(g18,g16)
    c: Equal(g16,g20)
    c: Equal(g20,g22)
    c: Equal(g22,g26)
    c: Equal(g26,g24)
    c: Equal(g24,g28)
    c: Equal(g28,g30)
    c: Equal(g25,g27)
    c: Equal(g27,g31)
    c: Equal(g31,g29)
    c: Equal(g29,g17)
    c: Equal(g17,g19)
    c: Equal(g19,g23)
    c: Equal(g23,g21)
    c: Symmetric(g16,g20,g-1)
    c: Symmetric(g24,g28,g-1)
    c: Symmetric(g26,g18,g-2)
    c: DistanceX(g18,g18) = 2.54
    c: DistanceY(g17,g17) = 0.762
    c: DistanceX(g17,g25) = 128.778
    c: DistanceY(g20,g16) = 10.16
    c: Symmetric(g8,g12,g-2)
    c: Symmetric(g1,g4,g-2)
    c: Symmetric(g1,g8,g-1)
    c: Equal(g0,g2)
    c: Equal(g2,g6)
    c: Equal(g6,g4)
    c: Equal(g4,g8)
    c: Equal(g8,g10)
    c: Equal(g10,g14)
    c: Equal(g14,g12)
    c: Equal(g9,g11)
    c: Equal(g11,g15)
    c: Equal(g15,g13)
    c: Equal(g13,g3)
    c: Equal(g3,g1)
    c: Equal(g1,g7)
    c: Equal(g7,g5)
    c: DistanceX(g0,g0) = 0.762
    c: DistanceY(g3,g3) = 2.54
    c: DistanceX(g0,g6) = 10.16
    c: DistanceY(g13,g5) = 67.818
FEATURE [PartDesign::Pocket] Pocket
  Length = 12.7
  Placement = pos=(0,0,8.636) rot=(0,0,1;0rad)
  Sketch = -> Sketch013
  Type = 0
FEATURE [Sketcher::SketchObject] Sketch015
  Placement = pos=(0,0,5.4356) rot=(0,0,1;0rad)
  expr: Constraints[11] = 4.8in + 0.05in
  expr: Constraints[10] = 2.4in + 0.05in
  sketch-geometry (4):
    g0: LineSegment StartX=-61.595 StartY=31.115 StartZ=0 EndX=61.595 EndY=31.115 EndZ=0
    g1: LineSegment StartX=61.595 StartY=31.115 StartZ=0 EndX=61.595 EndY=-31.115 EndZ=0
    g2: LineSegment StartX=61.595 StartY=-31.115 StartZ=0 EndX=-61.595 EndY=-31.115 EndZ=0
    g3: LineSegment StartX=-61.595 StartY=-31.115 StartZ=0 EndX=-61.595 EndY=31.115 EndZ=0
  constraints (12):
    c: Coincident(g0,g1)
    c: Coincident(g1,g2)
    c: Coincident(g2,g3)
    c: Coincident(g3,g0)
    c: Horizontal(g0)
    c: Horizontal(g2)
    c: Vertical(g1)
    c: Vertical(g3)
    c: Symmetric(g0,g0,g-2)
    c: Symmetric(g0,g2,g-1)
    c: DistanceY(g3,g3) = 62.23
    c: DistanceX(g0,g0) = 123.19
FEATURE [PartDesign::Pad] Pad012
  Length = 3.048
  Length2 = 100
  Placement = pos=(0,0,5.4356) rot=(0,0,1;0rad)
  Reversed = true
  Sketch = -> Sketch015
  Type = 0
FEATURE [Sketcher::SketchObject] Sketch014
  Placement = pos=(0,0,5.4356) rot=(0,0,1;0rad)
  Support = -> Pad012 [Face5]
  expr: Constraints[14] = 2.4in - 0.15in
  expr: Constraints[15] = 1.2in - 0.15in
  sketch-geometry (6):
    g0: LineSegment StartX=-60.579 StartY=30.099 StartZ=0 EndX=-53.721 EndY=30.099 EndZ=0
    g1: LineSegment StartX=-53.721 StartY=30.099 StartZ=0 EndX=-53.721 EndY=23.241 EndZ=0
    g2: LineSegment StartX=-53.721 StartY=23.241 StartZ=0 EndX=-60.579 EndY=23.241 EndZ=0
    g3: LineSegment StartX=-60.579 StartY=23.241 StartZ=0 EndX=-60.579 EndY=30.099 EndZ=0
    g4: LineSegment [constr] StartX=-60.579 StartY=30.099 StartZ=0 EndX=-53.721 EndY=23.241 EndZ=0
    g5: LineSegment [constr] StartX=-53.721 StartY=30.099 StartZ=0 EndX=-57.15 EndY=26.67 EndZ=0
  constraints (17):
    c: Coincident(g0,g1)
    c: Coincident(g1,g2)
    c: Coincident(g2,g3)
    c: Coincident(g3,g0)
    c: Horizontal(g0)
    c: Horizontal(g2)
    c: Vertical(g1)
    c: Vertical(g3)
    c: Equal(g0,g3)
    c: DistanceX(g0,g0) = 6.858
    c: Coincident(g4,g1)
    c: Coincident(g0,g4)
    c: Coincident(g0,g5)
    c: PointOnObject(g5,g4)
    c: DistanceX(g5,g-1) = 57.15
    c: DistanceY(g-1,g5) = 26.67
    c: Angle(g4,g5) = 1.5708
FEATURE [PartDesign::Pocket] Pocket001
  Length = 4.99999
  Placement = pos=(0,0,5.4356) rot=(0,0,1;0rad)
  Sketch = -> Sketch014
  Type = 1
FEATURE [PartDesign::LinearPattern] LinearPattern
  Direction = -> Sketch014 [H_Axis]
  Length = 114.3
  Occurrences = 16
  Placement = pos=(0,0,5.4356) rot=(0,0,1;0rad)
FEATURE [PartDesign::LinearPattern] LinearPattern001
  Direction = -> Sketch014 [V_Axis]
  Length = 53.34
  Occurrences = 8
  Placement = pos=(0,0,5.4356) rot=(0,0,1;0rad)
  Reversed = true
FEATURE [PartDesign::MultiTransform] MultiTransform
  Originals = -> [Pocket001]
  Placement = pos=(0,0,5.4356) rot=(0,0,1;0rad)
  Transformations = -> [LinearPattern,LinearPattern001]
FEATURE [Sketcher::SketchObject] Sketch016
  ExternalGeometry = -> [MultiTransform]
  Placement = pos=(0,0,5.4356) rot=(0,0,1;0rad)
  Support = -> MultiTransform [Face4]
  sketch-geometry (8):
    g0: LineSegment StartX=-61.595 StartY=31.115 StartZ=0 EndX=61.595 EndY=31.115 EndZ=0
    g1: LineSegment StartX=61.595 StartY=31.115 StartZ=0 EndX=61.595 EndY=-31.115 EndZ=0
    g2: LineSegment StartX=61.595 StartY=-31.115 StartZ=0 EndX=-61.595 EndY=-31.115 EndZ=0
    g3: LineSegment StartX=-61.595 StartY=-31.115 StartZ=0 EndX=-61.595 EndY=31.115 EndZ=0
    g4: LineSegment StartX=-62.23 StartY=31.75 StartZ=0 EndX=62.23 EndY=31.75 EndZ=0
    g5: LineSegment StartX=62.23 StartY=31.75 StartZ=0 EndX=62.23 EndY=-31.75 EndZ=0
    g6: LineSegment StartX=62.23 StartY=-31.75 StartZ=0 EndX=-62.23 EndY=-31.75 EndZ=0
    g7: LineSegment StartX=-62.23 StartY=-31.75 StartZ=0 EndX=-62.23 EndY=31.75 EndZ=0
  constraints (22):
    c: Coincident(g0,g1)
    c: Coincident(g1,g2)
    c: Coincident(g2,g3)
    c: Coincident(g3,g0)
    c: Horizontal(g0)
    c: Horizontal(g2)
    c: Vertical(g1)
    c: Vertical(g3)
    c: Coincident(g4,g5)
    c: Coincident(g5,g6)
    c: Coincident(g6,g7)
    c: Coincident(g7,g4)
    c: Horizontal(g4)
    c: Horizontal(g6)
    c: Vertical(g5)
    c: Vertical(g7)
    c: DistanceX(g4,g0) = 0.635
    c: DistanceY(g0,g4) = 0.635
    c: Coincident(g0,g-3)
    c: Coincident(g1,g-4)
    c: Symmetric(g5,g6,g-2)
    c: Symmetric(g4,g6,g-1)
FEATURE [PartDesign::Pad] Pad013
  Length = 10.16
  Length2 = 100
  Placement = pos=(0,0,5.4356) rot=(0,0,1;0rad)
  Reversed = true
  Sketch = -> Sketch016
  Type = 0
FEATURE [Sketcher::SketchObject] Sketch017
  Placement = pos=(0,0,5.4356) rot=(0,0,1;0rad)
  Support = -> Pad013 [Face7]
  sketch-geometry (23):
    g0: Circle CenterX=0 CenterY=0 CenterZ=0 NormalX=0 NormalY=0 NormalZ=1 Radius=1.397
    g1: Circle CenterX=0 CenterY=15.24 CenterZ=0 NormalX=0 NormalY=0 NormalZ=1 Radius=1.397
    g2: Circle CenterX=0 CenterY=-15.24 CenterZ=0 NormalX=0 NormalY=0 NormalZ=1 Radius=1.397
    g3: Circle CenterX=60.96 CenterY=15.24 CenterZ=0 NormalX=0 NormalY=0 NormalZ=1 Radius=1.397
    g4: Circle CenterX=60.96 CenterY=0 CenterZ=0 NormalX=0 NormalY=0 NormalZ=1 Radius=1.397
    g5: Circle CenterX=60.96 CenterY=-15.24 CenterZ=0 NormalX=0 NormalY=0 NormalZ=1 Radius=1.397
    g6: Circle CenterX=45.72 CenterY=-30.48 CenterZ=0 NormalX=0 NormalY=0 NormalZ=1 Radius=1.397
    g7: Circle CenterX=30.48 CenterY=-30.48 CenterZ=0 NormalX=0 NormalY=0 NormalZ=1 Radius=1.397
    g8: Circle CenterX=15.24 CenterY=-30.48 CenterZ=0 NormalX=0 NormalY=0 NormalZ=1 Radius=1.397
    g9: Circle CenterX=15.24 CenterY=30.48 CenterZ=0 NormalX=0 NormalY=0 NormalZ=1 Radius=1.397
    g10: Circle CenterX=30.48 CenterY=30.48 CenterZ=0 NormalX=0 NormalY=0 NormalZ=1 Radius=1.397
    g11: Circle CenterX=45.72 CenterY=30.48 CenterZ=0 NormalX=0 NormalY=0 NormalZ=1 Radius=1.397
    g12: Circle CenterX=-30.48 CenterY=30.48 CenterZ=0 NormalX=0 NormalY=0 NormalZ=1 Radius=1.397
    g13: Circle CenterX=-45.72 CenterY=30.48 CenterZ=0 NormalX=0 NormalY=0 NormalZ=1 Radius=1.397
    g14: Circle CenterX=0 CenterY=30.48 CenterZ=0 NormalX=0 NormalY=0 NormalZ=1 Radius=1.397
    g15: Circle CenterX=-45.72 CenterY=-30.48 CenterZ=0 NormalX=0 NormalY=0 NormalZ=1 Radius=1.397
    g16: Circle CenterX=-30.48 CenterY=-30.48 CenterZ=0 NormalX=0 NormalY=0 NormalZ=1 Radius=1.397
    g17: Circle CenterX=-15.24 CenterY=-30.48 CenterZ=0 NormalX=0 NormalY=0 NormalZ=1 Radius=1.397
    g18: Circle CenterX=-60.96 CenterY=15.24 CenterZ=0 NormalX=0 NormalY=0 NormalZ=1 Radius=1.397
    g19: Circle CenterX=-60.96 CenterY=0 CenterZ=0 NormalX=0 NormalY=0 NormalZ=1 Radius=1.397
    g20: Circle CenterX=-60.96 CenterY=-15.24 CenterZ=0 NormalX=0 NormalY=0 NormalZ=1 Radius=1.397
    g21: Circle CenterX=-15.24 CenterY=30.48 CenterZ=0 NormalX=0 NormalY=0 NormalZ=1 Radius=1.397
    g22: Circle CenterX=0 CenterY=-30.48 CenterZ=0 NormalX=0 NormalY=0 NormalZ=1 Radius=1.397
  constraints (60):
    c: Symmetric(g21,g9,g-2)
    c: Symmetric(g12,g10,g-2)
    c: Symmetric(g13,g11,g-2)
    c: Symmetric(g17,g8,g-2)
    c: Symmetric(g16,g7,g-2)
    c: Symmetric(g6,g15,g-2)
    c: Symmetric(g18,g20,g-1)
    c: Symmetric(g3,g5,g-1)
    c: PointOnObject(g14,g-2)
    c: PointOnObject(g22,g-2)
    c: PointOnObject(g19,g-1)
    c: DistanceY(g21,g14) = 0
    c: DistanceY(g21,g12) = 0
    c: DistanceY(g13,g12) = 0
    c: DistanceY(g22,g17) = 0
    c: DistanceY(g17,g16) = 0
    c: DistanceY(g16,g15) = 0
    c: DistanceX(g19,g20) = 0
    c: DistanceX(g5,g4) = 0
    c: DistanceY(g-1,g18) = 15.24
    c: DistanceY(g4,g3) = 15.24
    c: DistanceX(g21,g14) = 15.24
    c: DistanceX(g12,g21) = 15.24
    c: DistanceX(g13,g12) = 15.24
    c: DistanceX(g17,g22) = 15.24
    c: DistanceX(g16,g17) = 15.24
    c: DistanceX(g15,g16) = 15.24
    c: PointOnObject(g4,g-1)
    c: Symmetric(g14,g22,g-1)
    c: Symmetric(g19,g4,g-2)
    c: DistanceY(g-1,g14) = 30.48
    c: DistanceX(g-1,g4) = 60.96
    c: Symmetric(g2,g1,g-1)
    c: PointOnObject(g0,g-1)
    c: DistanceX(g2,g0) = 0
    c: PointOnObject(g0,g-2)
    c: DistanceY(g-1,g1) = 15.24
    c: Equal(g18,g19)
    c: Equal(g19,g20)
    c: Equal(g20,g15)
    c: Equal(g15,g16)
    c: Equal(g16,g17)
    c: Equal(g17,g22)
    c: Equal(g22,g8)
    c: Equal(g8,g7)
    c: Equal(g7,g6)
    c: Equal(g6,g5)
    c: Equal(g5,g4)
    c: Equal(g4,g3)
    c: Equal(g3,g11)
    c: Equal(g11,g10)
    c: Equal(g10,g9)
    c: Equal(g9,g14)
    c: Equal(g14,g21)
    c: Equal(g21,g12)
    c: Equal(g12,g13)
    c: Equal(g13,g1)
    c: Equal(g1,g0)
    c: Equal(g0,g2)
    c: Radius(g0) = 1.397
FEATURE [PartDesign::Pad] Pad014
  Length = 6.604
  Length2 = 100
  Placement = pos=(0,0,5.4356) rot=(0,0,1;0rad)
  Reversed = true
  Sketch = -> Sketch017
  Type = 0
FEATURE [App::DocumentObjectGroup] Group004  label="baffle"
  Group = -> [ultim8x8baffles,Pad012,Pocket001,MultiTransform,Pad013,Pad014]
FEATURE [Sketcher::SketchObject] Sketch018
  ExternalGeometry = -> [Pocket]
  Placement = pos=(0,33.909,8.636) rot=(0,0.707107,0.707107;3.14159rad)
  Support = -> Pocket [Face14]
  sketch-geometry (4):
    g0: LineSegment StartX=46.355 StartY=-40.64 StartZ=0 EndX=29.591 EndY=-40.64 EndZ=0
    g1: LineSegment StartX=29.591 StartY=-40.64 StartZ=0 EndX=29.591 EndY=-29.464 EndZ=0
    g2: LineSegment StartX=29.591 StartY=-29.464 StartZ=0 EndX=46.355 EndY=-29.464 EndZ=0
    g3: LineSegment StartX=46.355 StartY=-29.464 StartZ=0 EndX=46.355 EndY=-40.64 EndZ=0
  constraints (12):
    c: Coincident(g0,g1)
    c: Coincident(g1,g2)
    c: Coincident(g2,g3)
    c: Coincident(g3,g0)
    c: Horizontal(g0)
    c: Horizontal(g2)
    c: Vertical(g1)
    c: Vertical(g3)
    c: DistanceX(g2,g2) = 16.764
    c: DistanceY(g1,g1) = 11.176
    c: DistanceY(g-3,g0) = 0
    c: DistanceX(g0,g-3) = 16.002
FEATURE [PartDesign::Pocket] Pocket002
  Length = 4.99999
  Placement = pos=(0,0,8.636) rot=(0,0,1;0rad)
  Sketch = -> Sketch018
  Type = 2
FEATURE [PartDesign::Fillet] Fillet002
  Base = -> Pocket002 [Edge96,Edge98,Edge100,Edge102]
  Placement = pos=(0,0,8.636) rot=(0,0,1;0rad)
  Radius = 2.032
FEATURE [App::DocumentObjectGroup] Group  label="case"
  Group = -> [Pad002,Pad003,Pad008,Pad009,Pad010,Fillet001,Pocket,Pocket002,Fillet002]
